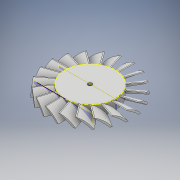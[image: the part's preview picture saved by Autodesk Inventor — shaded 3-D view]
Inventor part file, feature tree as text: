
AUTODESK INVENTOR PART (.ipt)
format: ipt  version: 2018 (Build 220112000, 112)  size: 463,872 bytes
history: native  units: mm
features: sketch x6, extrude x3, plane x2, sweep x1, pattern_circular x1
ambient origin geometry x8: Origin, YZ Plane, XZ Plane, XY Plane, X Axis, Y Axis, Z Axis, Center Point
bodies: Solid1 (feature_tree)
feature tree (13):
  extrude  "Extrusion1"  Depth=25.0mm
  sketch  "Sketch2"  dims[d3=2.0mm d4=2.0mm]
  plane  "Work Plane1"
  sweep  "Sweep1"
  extrude  "Extrusion2"  Depth=8.0mm
  pattern_circular  "Circular Pattern1"  Count=20 Angle=360.0deg
  plane  "Work Plane3"
  extrude  "Extrusion3"  Depth=3.0mm TaperAngle=0.0deg
  sketch  "Sketch1"  dims[d0=2.1mm d1=25.0mm]
  sketch  "Sketch3"  dims[d5=5.0mm d6=0.0mm d13=8.0mm]
  sketch  "Sketch5"  dims[d14=0.0mm d15=0.872665mm]
  sketch  "Sketch6"  dims[d16=1.0mm d17=0.0mm d18=200.0mm d19=360.0deg]
  sketch  "Sketch9"  dims[d21=12.5mm d22=3.0mm d23=0.0mm]
